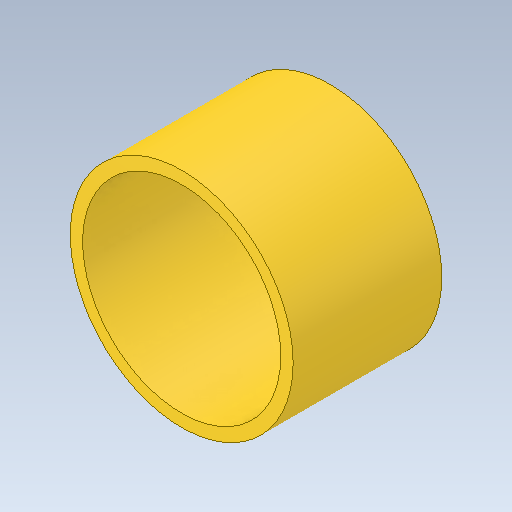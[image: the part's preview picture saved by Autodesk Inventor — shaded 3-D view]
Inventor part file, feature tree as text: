
AUTODESK INVENTOR PART (.ipt)
format: ipt  version: 2020.1 (Build 241239000, 239)  size: 113,152 bytes
history: native  units: mm
features: extrude x1, sketch x1
ambient origin geometry x8: Origin, YZ Plane, XZ Plane, XY Plane, X Axis, Y Axis, Z Axis, Center Point
bodies: Solid1 (feature_tree)
feature tree (2):
  extrude  "Extrusion1"  Depth=6.0mm
  sketch  "Sketch1"  dims[d0=8.0mm d1=9.0mm d2=6.0mm d3=0.0mm]
